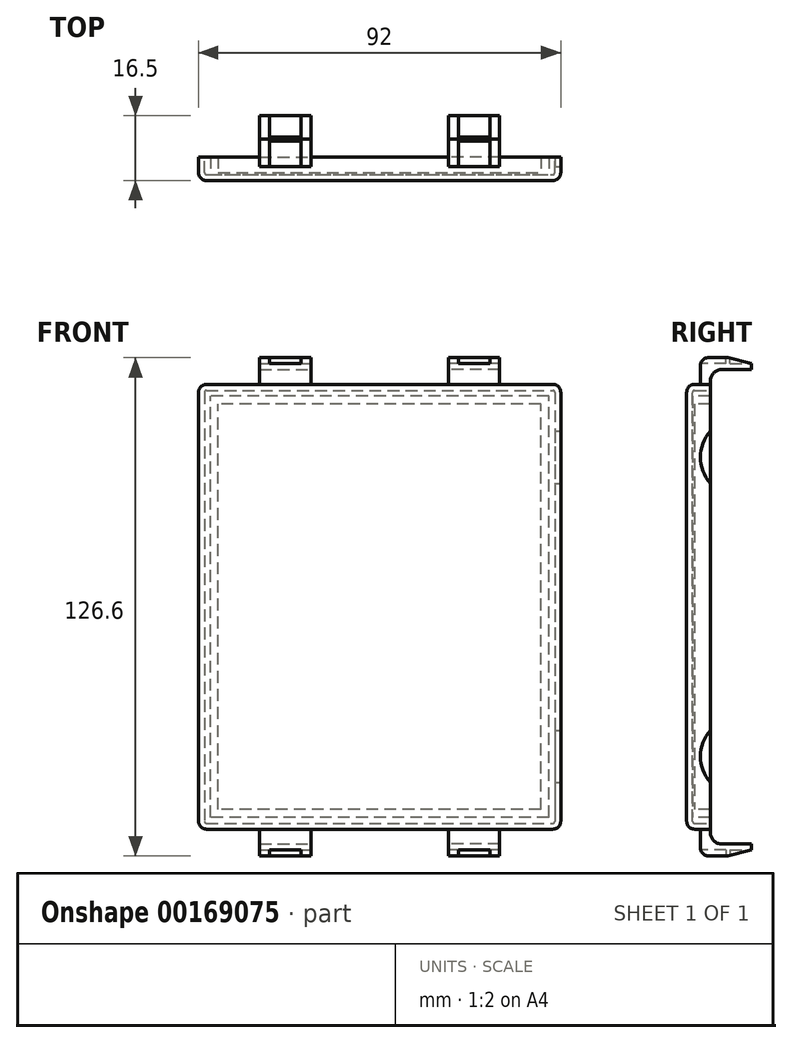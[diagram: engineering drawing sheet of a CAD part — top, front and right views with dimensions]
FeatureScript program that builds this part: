
annotation { "Feature Type Name" : "Feature", "Feature Type Description" : "" }
export const myFeature = defineFeature(function(context is Context, id is Id, definition is map)
    precondition{}
    {
        {
            var Q0;
            Q0=qCreatedBy(makeId("Front.planeOp"),FACE);
            var sketch = newSketch(context, id + "F0", { "sketchPlane" : qUnion([Q0])});
            skLineSegment(sketch, "E0.bottom", {"start": v(-46, 56.5) * mm, "end": v(46, 56.5) * mm});
            skLineSegment(sketch, "E0.top", {"start": v(-46, -56.5) * mm, "end": v(46, -56.5) * mm});
            skLineSegment(sketch, "E0.left", {"start": v(-46, 56.5) * mm, "end": v(-46, -56.5) * mm});
            skLineSegment(sketch, "E0.right", {"start": v(46, 56.5) * mm, "end": v(46, -56.5) * mm});
            skLineSegment(sketch, "E1", {"start": v(0, 56.5) * mm, "end": v(0, 0) * mm, "construction": true});
            skLineSegment(sketch, "E2", {"start": v(0, 0) * mm, "end": v(46, 0) * mm, "construction": true});
            skSolve(sketch);
        }
        {
            var Q0;
            Q0 = qSketchRegion(id + "F0", true);
            extrude(context, id + "F1", {"entities" : qUnion([Q0]), "endBound" : BoundingType.SYMMETRIC, "depth" : 6 * mm});
        }
        {
            var Q0;
            Q0=makeQuery(id+"F1.opExtrude","CAP_FACE",FACE,{"disambiguationData":[OSD([sQuery(id+"F0.wireOp",EDGE,"E0.bottom"),sQuery(id+"F0.wireOp",EDGE,"E0.top"),sQuery(id+"F0.wireOp",EDGE,"E0.left"),sQuery(id+"F0.wireOp",EDGE,"E0.right")])],"isStart":false});
            var Q1;
            Q1=makeQuery(id+"F1.opExtrude","SWEPT_EDGE",EDGE,{"disambiguationData":[OSD([sQuery(id+"F0.wireOp",EDGE,"E0.bottom"),sQuery(id+"F0.wireOp",EDGE,"E0.right")])]});
            var Q2;
            Q2=makeQuery(id+"F1.opExtrude","SWEPT_EDGE",EDGE,{"disambiguationData":[OSD([sQuery(id+"F0.wireOp",EDGE,"E0.bottom"),sQuery(id+"F0.wireOp",EDGE,"E0.left")])]});
            var Q3;
            Q3=makeQuery(id+"F1.opExtrude","SWEPT_EDGE",EDGE,{"disambiguationData":[OSD([sQuery(id+"F0.wireOp",EDGE,"E0.top"),sQuery(id+"F0.wireOp",EDGE,"E0.right")])]});
            var Q4;
            Q4=makeQuery(id+"F1.opExtrude","SWEPT_EDGE",EDGE,{"disambiguationData":[OSD([sQuery(id+"F0.wireOp",EDGE,"E0.top"),sQuery(id+"F0.wireOp",EDGE,"E0.left")])]});
            fillet(context, id + "F2", {"entities" : qUnion([Q0, Q1, Q2, Q3, Q4]), "radius" : 2 * mm, "tangentPropagation" : true, "allowEdgeOverflow" : false});
        }
        {
            var Q0;
            Q0=makeQuery(id+"F1.opExtrude","CAP_FACE",FACE,{"disambiguationData":[OSD([sQuery(id+"F0.wireOp",EDGE,"E0.bottom"),sQuery(id+"F0.wireOp",EDGE,"E0.top"),sQuery(id+"F0.wireOp",EDGE,"E0.left"),sQuery(id+"F0.wireOp",EDGE,"E0.right")])],"isStart":true});
            shell(context, id + "F3", {"entities" : qUnion([Q0]), "thickness" : 1.5 * mm});
        }
        {
            var Q0;
            Q0=makeQuery(id+"F3.opShell","OFFSET_FACE",FACE,{"disambiguationData":[OSD([sQuery(id+"F0.wireOp",EDGE,"E0.bottom"),sQuery(id+"F0.wireOp",EDGE,"E0.top"),sQuery(id+"F0.wireOp",EDGE,"E0.left"),sQuery(id+"F0.wireOp",EDGE,"E0.right")])]});
            var sketch = newSketch(context, id + "F4", { "sketchPlane" : qUnion([Q0])});
            skLineSegment(sketch, "E3.0", {"start": v(43, 53.5) * mm, "end": v(-43, 53.5) * mm});
            skLineSegment(sketch, "E3.1", {"start": v(43, 53.5) * mm, "end": v(43, -53.5) * mm});
            skLineSegment(sketch, "E3.2", {"start": v(43, -53.5) * mm, "end": v(-43, -53.5) * mm});
            skLineSegment(sketch, "E3.3", {"start": v(-43, 53.5) * mm, "end": v(-43, -53.5) * mm});
            skSolve(sketch);
        }
        {
            var Q0;
            Q0 = qSketchRegion(id + "F4", true);
            var Q1;
            Q1=makeQuery(id+"F1.opExtrude","CAP_FACE",FACE,{"disambiguationData":[OSD([sQuery(id+"F0.wireOp",EDGE,"E0.bottom"),sQuery(id+"F0.wireOp",EDGE,"E0.top"),sQuery(id+"F0.wireOp",EDGE,"E0.left"),sQuery(id+"F0.wireOp",EDGE,"E0.right")])],"isStart":true});
            extrude(context, id + "F5", {"entities" : qUnion([Q0]), "operationType" : NewBodyOperationType.ADD, "endBound" : BoundingType.UP_TO_SURFACE, "endBoundEntityFace" : qUnion([Q1]), "depth" : 25.4 * mm});
        }
        {
            var Q0;
            Q0=makeQuery(id+"F5.opExtrude","CAP_FACE",FACE,{"disambiguationData":[OSD([sQuery(id+"F4.wireOp",EDGE,"E3.0"),sQuery(id+"F4.wireOp",EDGE,"E3.1"),sQuery(id+"F4.wireOp",EDGE,"E3.2"),sQuery(id+"F4.wireOp",EDGE,"E3.3")])],"isStart":false});
            shell(context, id + "F6", {"entities" : qUnion([Q0]), "thickness" : 2 * mm});
        }
        {
            var Q0;
            Q0=qCreatedBy(makeId("Right.planeOp"),FACE);
            cPlane(context, id + "F7", {"entities" : qUnion([Q0]), "cplaneType" : CPlaneType.OFFSET, "offset" : 24 * mm, "width" : 152.4 * mm, "height" : 152.4 * mm});
        }
        {
            var Q0;
            Q0=qCreatedBy(id+"F7.planeOp",FACE);
            var sketch = newSketch(context, id + "F8", { "sketchPlane" : qUnion([Q0])});
            skLineSegment(sketch, "E4", {"start": v(0.5, 55.5) * mm, "end": v(0.5, 61.3) * mm});
            skLineSegment(sketch, "E5", {"start": v(2.5, 63.3) * mm, "end": v(7.5, 63.3) * mm});
            skLineSegment(sketch, "E6", {"start": v(7.5, 63.3) * mm, "end": v(13.5, 61.8) * mm});
            skLineSegment(sketch, "E7", {"start": v(13.5, 61.8) * mm, "end": v(13.5, 60.3) * mm});
            skLineSegment(sketch, "E8", {"start": v(13.5, 60.3) * mm, "end": v(6, 60.3) * mm});
            skLineSegment(sketch, "E9", {"start": v(3, 57.3) * mm, "end": v(3, 55.5) * mm});
            skLineSegment(sketch, "E10", {"start": v(3, 55.5) * mm, "end": v(0.5, 55.5) * mm});
            skPoint(sketch, "E11.visualSharp", {"position": v(0.5, 63.3) * mm});
            skArc(sketch, "E11.filletArc", {"start": v(2.5, 63.3) * mm, "mid": v(1.09, 62.71) * mm, "end": v(0.5, 61.3) * mm});
            skPoint(sketch, "E12.visualSharp", {"position": v(3, 60.3) * mm});
            skArc(sketch, "E12.filletArc", {"start": v(6, 60.3) * mm, "mid": v(3.88, 59.42) * mm, "end": v(3, 57.3) * mm});
            skSolve(sketch);
        }
        {
            var Q0;
            Q0 = qSketchRegion(id + "F8", true);
            extrude(context, id + "F9", {"entities" : qUnion([Q0]), "operationType" : NewBodyOperationType.ADD, "endBound" : BoundingType.SYMMETRIC, "depth" : 13 * mm});
        }
        {
            var Q0;
            Q0=makeQuery(id+"F9.opExtrude","SWEPT_FACE",FACE,{"disambiguationData":[OSD([sQuery(id+"F8.wireOp",EDGE,"E5")])]});
            var sketch = newSketch(context, id + "F10", { "sketchPlane" : qUnion([Q0])});
            skLineSegment(sketch, "E13.bottom", {"start": v(20, 7) * mm, "end": v(28, 7) * mm});
            skLineSegment(sketch, "E13.top", {"start": v(20, 0) * mm, "end": v(28, 0) * mm});
            skLineSegment(sketch, "E13.left", {"start": v(20, 7) * mm, "end": v(20, 0) * mm});
            skLineSegment(sketch, "E13.right", {"start": v(28, 7) * mm, "end": v(28, 0) * mm});
            skLineSegment(sketch, "E14.bottom", {"start": v(20, 8) * mm, "end": v(28, 8) * mm});
            skLineSegment(sketch, "E14.top", {"start": v(20, 15.36) * mm, "end": v(28, 15.36) * mm});
            skLineSegment(sketch, "E14.left", {"start": v(20, 8) * mm, "end": v(20, 15.36) * mm});
            skLineSegment(sketch, "E14.right", {"start": v(28, 8) * mm, "end": v(28, 15.36) * mm});
            skSolve(sketch);
        }
        {
            var Q0;
            Q0 = qSketchRegion(id + "F10", true);
            extrude(context, id + "F11", {"entities" : qUnion([Q0]), "operationType" : NewBodyOperationType.REMOVE, "oppositeDirection" : true, "depth" : 1.5 * mm});
        }
        {
            var Q0;
            Q0=makeQuery(id+"F1.opExtrude","SWEPT_BODY",BODY,{"disambiguationData":[OSD([sQuery(id+"F0.wireOp",EDGE,"E0.bottom"),sQuery(id+"F0.wireOp",EDGE,"E0.top"),sQuery(id+"F0.wireOp",EDGE,"E0.left"),sQuery(id+"F0.wireOp",EDGE,"E0.right")])]});
            var Q1;
            Q1=qCreatedBy(makeId("Right.planeOp"),FACE);
            mirror(context, id + "F12", {"operationType" : NewBodyOperationType.ADD, "entities" : qUnion([Q0]), "mirrorPlane" : qUnion([Q1])});
        }
        {
            var Q0;
            Q0=makeQuery(id+"F1.opExtrude","SWEPT_BODY",BODY,{"disambiguationData":[OSD([sQuery(id+"F0.wireOp",EDGE,"E0.bottom"),sQuery(id+"F0.wireOp",EDGE,"E0.top"),sQuery(id+"F0.wireOp",EDGE,"E0.left"),sQuery(id+"F0.wireOp",EDGE,"E0.right")])]});
            var Q1;
            Q1=makeQuery(id+"F12.opPattern","COPY",BODY,{"derivedFrom":makeQuery(id+"F1.opExtrude","SWEPT_BODY",BODY,{"disambiguationData":[OSD([sQuery(id+"F0.wireOp",EDGE,"E0.bottom"),sQuery(id+"F0.wireOp",EDGE,"E0.top"),sQuery(id+"F0.wireOp",EDGE,"E0.left"),sQuery(id+"F0.wireOp",EDGE,"E0.right")])]}),"instanceName":"1"});
            var Q2;
            Q2=qCreatedBy(makeId("Top.planeOp"),FACE);
            mirror(context, id + "F13", {"operationType" : NewBodyOperationType.ADD, "entities" : qUnion([Q0, Q1]), "mirrorPlane" : qUnion([Q2])});
        }
        {
            var Q0;
            Q0=makeQuery(id+"F1.opExtrude","SWEPT_FACE",FACE,{"disambiguationData":[OSD([sQuery(id+"F0.wireOp",EDGE,"E0.right")])]});
            var sketch = newSketch(context, id + "F14", { "sketchPlane" : qUnion([Q0])});
            skCircle(sketch, "E15", {"center": v(10.5, 38) * mm, "radius": 10 * mm});
            skSolve(sketch);
        }
        {
            var Q0;
            Q0 = qSketchRegion(id + "F14", true);
            var Q1;
            Q1=makeQuery(id+"F5.opExtrude","SWEPT_FACE",FACE,{"disambiguationData":[OSD([sQuery(id+"F4.wireOp",EDGE,"E3.3")])]});
            extrude(context, id + "F15", {"entities" : qUnion([Q0]), "endBound" : BoundingType.UP_TO_SURFACE, "oppositeDirection" : true, "endBoundEntityFace" : qUnion([Q1]), "depth" : 25.4 * mm});
        }
        {
            var Q0;
            Q0=makeQuery(id+"F15.opExtrude","SWEPT_BODY",BODY,{"disambiguationData":[OSD([sQuery(id+"F14.wireOp",EDGE,"E15")])]});
            var Q1;
            Q1=qCreatedBy(makeId("Top.planeOp"),FACE);
            mirror(context, id + "F16", {"entities" : qUnion([Q0]), "mirrorPlane" : qUnion([Q1])});
        }
        {
            var Q0;
            Q0=makeQuery(id+"F15.opExtrude","SWEPT_BODY",BODY,{"disambiguationData":[OSD([sQuery(id+"F14.wireOp",EDGE,"E15")])]});
            var Q1;
            Q1=makeQuery(id+"F16.opPattern","COPY",BODY,{"derivedFrom":makeQuery(id+"F15.opExtrude","SWEPT_BODY",BODY,{"disambiguationData":[OSD([sQuery(id+"F14.wireOp",EDGE,"E15")])]}),"instanceName":"1"});
            var Q2;
            Q2=makeQuery(id+"F1.opExtrude","SWEPT_BODY",BODY,{"disambiguationData":[OSD([sQuery(id+"F0.wireOp",EDGE,"E0.bottom"),sQuery(id+"F0.wireOp",EDGE,"E0.top"),sQuery(id+"F0.wireOp",EDGE,"E0.left"),sQuery(id+"F0.wireOp",EDGE,"E0.right")])]});
            booleanBodies(context, id + "F17", {"operationType" : BooleanOperationType.SUBTRACTION, "tools" : qUnion([Q0, Q1]), "targets" : qUnion([Q2])});
        }
    });
